# Revit family: Trap-ForBasins-Vitra-OtherSeries-A45149
name_source: partatom
category: Plumbing Fixtures
revit_build: Autodesk Revit 2017 (Build: 20160225_1515(x64)
units: mm (PartAtom-declared; Revit-internal decimal feet)

## family parameters
Always vertical = No
Cut with Voids When Loaded = No
OmniClass Number = 23.45.00.00
OmniClass Title = Sanitary, Laundry, and Cleaning Equipment
Part Type = Normal
Room Calculation Point = No
Round Connector Dimension = Use Diameter
Shared = Yes
Work Plane-Based = Yes

## types (4) — shared parameters
BIMobject category = Sanitary - Taps & Mixers
Brand = VitrA
CW Connection = No
Default Elevation = 600 mm
Description = Waste Sets Waste Set Universal (Push-Open)
Design country = Turkey
HW Connection = No
Hot Water Supply (max.) = 80 °C
Hot Water temperature, factory set to = 38 °C
IFC Classification = Sanitary Terminal
Main Material = Metal
Manufacturer = Vitra
Manufacturer name = Vitra
Masterformat 2014 Code = 22 13 16
Masterformat 2014 Description = Sanitary Waste and Vent Piping
Min. flow pressure of = 0.5 bar
Mounting type = Washbasin Connect
NBS Referans Code = 31-76
NBS Referans Description = Sanitary Dispensing And Disposal Units
Nominal Depth (mm) = 65 mm  [stored 0.213255 ft]
Nominal Height (mm) = 125 mm  [stored 0.410105 ft]
Nominal Width (mm) = 65 mm  [stored 0.213255 ft]
OmniClass Code = 23-21 23 27
OmniClass Description = Residential Waste Disposal Units
Product Properties = Push-Open
Product Type = Waste Sets Waste Set Universal
Product certification = https://www.vitraglobal.com
Product family = Other
Product group = Other Trap
Product url = https://www.vitraglobal.com
Range of Hot Water Supply = 5 - 65 °C
Range of flow pressure = 1 - 5 bar
Test Pressure = 16 bar
UNSPSC Description = Sanitary ware
URL = https://vitraglobal.com
Uniclass 1.4 Code = L7218
Uniclass 1.4 Description = Sanitary disposal units
Uniclass 2.0 Code = PR-31-76
Uniclass 2.0 Description = Sanitary Dispensing And Disposal Units
Uniclass 2015 Code = Pr_60_45_90
Uniclass 2015 Name = Wastewater and water mixer products
Uniformat II Code = D2010
Uniformat II Description = Plumbing Fixtures
Vent Connection = No
Warranty Period (Year) = 5
Waste Connection = Yes
Weight Net (kg) = 0.5
Youtube = https://www.youtube.com

## per-type parameters (varying)
| type | Article No. (default) | Coating Material | Color | Model | Product SKU | Technical description |
| Trap-ForBasins-Vitra-OtherSeries-A45149 | A45149 | Chrome | Chrome | A45149 | A45149 | https://vitraglobal.com |
| Trap-ForBasins-Vitra-OtherSeries-A4514934 | A4514934 | Brushed Nickel (Metal) | Brushed Nickel | A4514934 | A4514934 | https://vitraglobal.com |
| Trap-ForBasins-Vitra-OtherSeries-A4514936 | A4514936 | Matte Black (Metal) | Matte Black | A4514936 | A4514936 | https://vitraglobal.com |
| Trap-ForBasins-Vitra-OtherSeries-A4514926 | A4514926 | Copper (Metal) | Copper | A4514926 | A4514926 | https://www.vitraglobal.com |

note: [stored X ft] marks values corroborated as IEEE doubles in the binary element streams (Revit-internal decimal feet)

## geometry (parser evidence)
native form markers: Sweep x2
no freeform markers — native parametric forms only
